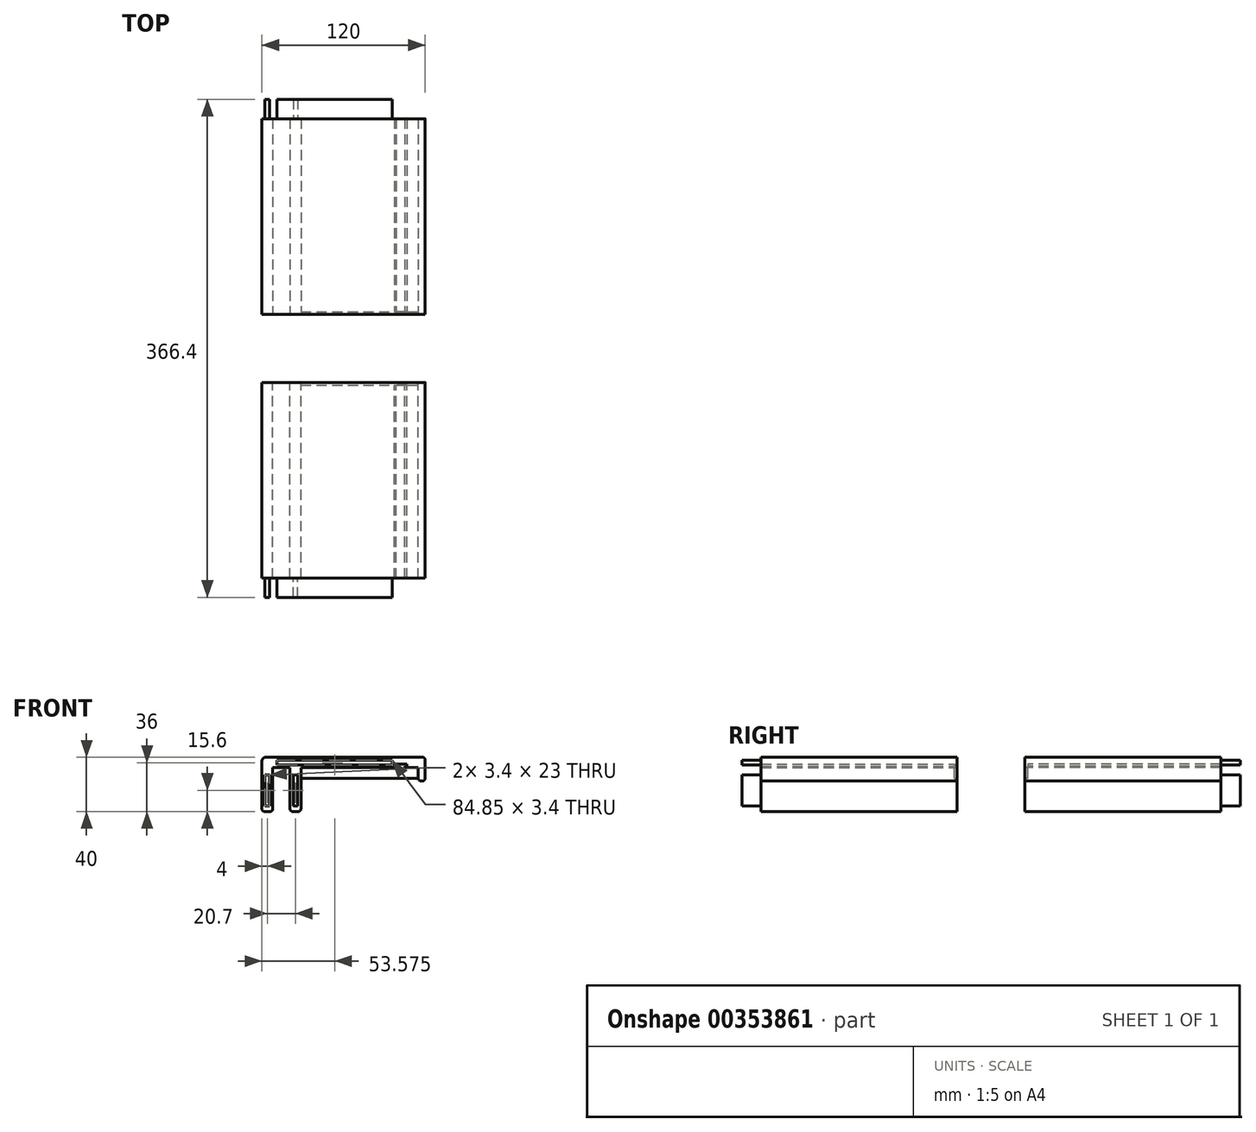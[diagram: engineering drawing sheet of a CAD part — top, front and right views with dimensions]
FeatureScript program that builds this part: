
annotation { "Feature Type Name" : "Feature", "Feature Type Description" : "" }
export const myFeature = defineFeature(function(context is Context, id is Id, definition is map)
    precondition{}
    {
        {
            var Q0;
            Q0=qCreatedBy(makeId("Front.planeOp"),FACE);
            var sketch = newSketch(context, id + "F0", { "sketchPlane" : qUnion([Q0])});
            skLineSegment(sketch, "E0", {"start": v(0, 2) * mm, "end": v(0, 37) * mm});
            skLineSegment(sketch, "E1", {"start": v(3, 40) * mm, "end": v(118, 40) * mm});
            skLineSegment(sketch, "E2", {"start": v(105, 32.4) * mm, "end": v(105, 33.4) * mm});
            skLineSegment(sketch, "E3", {"start": v(105, 33.4) * mm, "end": v(106.75, 33.4) * mm});
            skLineSegment(sketch, "E4", {"start": v(106.75, 33.4) * mm, "end": v(106.75, 34.8) * mm});
            skLineSegment(sketch, "E5", {"start": v(106.75, 34.8) * mm, "end": v(97.45, 34.8) * mm});
            skLineSegment(sketch, "E6", {"start": v(97.45, 34.8) * mm, "end": v(97.45, 33.4) * mm});
            skLineSegment(sketch, "E7", {"start": v(97.45, 33.4) * mm, "end": v(98.7, 33.4) * mm});
            skLineSegment(sketch, "E8", {"start": v(98.7, 33.4) * mm, "end": v(98.7, 32.4) * mm});
            skLineSegment(sketch, "E9", {"start": v(98.7, 32.4) * mm, "end": v(28.7, 32.4) * mm});
            skLineSegment(sketch, "E10", {"start": v(28.7, 32.4) * mm, "end": v(28.7, 2) * mm});
            skLineSegment(sketch, "E11", {"start": v(26.7, 0) * mm, "end": v(22.7, 0) * mm});
            skLineSegment(sketch, "E12", {"start": v(20.7, 2) * mm, "end": v(20.7, 32.4) * mm});
            skLineSegment(sketch, "E13", {"start": v(20.7, 32.4) * mm, "end": v(8, 32.4) * mm});
            skLineSegment(sketch, "E14", {"start": v(8, 32.4) * mm, "end": v(8, 2) * mm});
            skLineSegment(sketch, "E15", {"start": v(6, 0) * mm, "end": v(2, 0) * mm});
            skLineSegment(sketch, "E16", {"start": v(105, 32.4) * mm, "end": v(120, 32.4) * mm});
            skLineSegment(sketch, "E17", {"start": v(120, 38) * mm, "end": v(120, 32.4) * mm});
            skLineSegment(sketch, "E18", {"start": v(120, 32.4) * mm, "end": v(120, 24.4) * mm});
            skLineSegment(sketch, "E19", {"start": v(118, 22.4) * mm, "end": v(117, 22.4) * mm});
            skLineSegment(sketch, "E20", {"start": v(115, 24.4) * mm, "end": v(115, 32.4) * mm});
            skPoint(sketch, "E21.visualSharp", {"position": v(0, 40) * mm});
            skArc(sketch, "E21.filletArc", {"start": v(3, 40) * mm, "mid": v(0.88, 39.12) * mm, "end": v(0, 37) * mm});
            skPoint(sketch, "E22.visualSharp", {"position": v(0, 0) * mm});
            skArc(sketch, "E22.filletArc", {"start": v(0, 2) * mm, "mid": v(0.59, 0.59) * mm, "end": v(2, 0) * mm});
            skPoint(sketch, "E23.visualSharp", {"position": v(8, 0) * mm});
            skArc(sketch, "E23.filletArc", {"start": v(6, 0) * mm, "mid": v(7.41, 0.59) * mm, "end": v(8, 2) * mm});
            skPoint(sketch, "E24.visualSharp", {"position": v(20.7, 0) * mm});
            skArc(sketch, "E24.filletArc", {"start": v(20.7, 2) * mm, "mid": v(21.29, 0.59) * mm, "end": v(22.7, 0) * mm});
            skPoint(sketch, "E25.visualSharp", {"position": v(28.7, 0) * mm});
            skArc(sketch, "E25.filletArc", {"start": v(26.7, 0) * mm, "mid": v(28.11, 0.59) * mm, "end": v(28.7, 2) * mm});
            skPoint(sketch, "E26.visualSharp", {"position": v(120, 22.4) * mm});
            skArc(sketch, "E26.filletArc", {"start": v(118, 22.4) * mm, "mid": v(119.41, 23) * mm, "end": v(120, 24.4) * mm});
            skPoint(sketch, "E27.visualSharp", {"position": v(115, 22.4) * mm});
            skArc(sketch, "E27.filletArc", {"start": v(115, 24.4) * mm, "mid": v(115.59, 23) * mm, "end": v(117, 22.4) * mm});
            skPoint(sketch, "E28.visualSharp", {"position": v(120, 40) * mm});
            skArc(sketch, "E28.filletArc", {"start": v(120, 38) * mm, "mid": v(119.41, 39.41) * mm, "end": v(118, 40) * mm});
            skSolve(sketch);
        }
        {
            var Q0;
            Q0=makeQuery(id+"F0.imprint","IMPRINT",FACE,{"disambiguationData":[TD([[makeQuery(id+"F0.imprint","IMPRINT",EDGE,{"derivedFrom":sQuery(id+"F0.wireOp",EDGE,"E0")}),-1.0]])]});
            var Q1;
            {var subQ1=sQuery(id+"F0.wireOp",EDGE,"E18");Q1=makeQuery(id+"F0.imprint","IMPRINT",FACE,{"disambiguationData":[TD([[makeQuery(id+"F0.imprint","IMPRINT",EDGE,{"derivedFrom":subQ1}),-1.0]])]});}
            extrude(context, id + "F1", {"entities" : qUnion([Q0, Q1]), "depth" : 144 * mm});
        }
        {
            var Q0;
            Q0=makeQuery(id+"F1.opExtrude","CAP_FACE",FACE,{"disambiguationData":[OSD([sQuery(id+"F0.wireOp",EDGE,"E0"),sQuery(id+"F0.wireOp",EDGE,"E1"),sQuery(id+"F0.wireOp",EDGE,"E2"),sQuery(id+"F0.wireOp",EDGE,"E3"),sQuery(id+"F0.wireOp",EDGE,"E4"),sQuery(id+"F0.wireOp",EDGE,"E5"),sQuery(id+"F0.wireOp",EDGE,"E6"),sQuery(id+"F0.wireOp",EDGE,"E7"),sQuery(id+"F0.wireOp",EDGE,"E8"),sQuery(id+"F0.wireOp",EDGE,"E9"),sQuery(id+"F0.wireOp",EDGE,"E10"),sQuery(id+"F0.wireOp",EDGE,"E11"),sQuery(id+"F0.wireOp",EDGE,"E12"),sQuery(id+"F0.wireOp",EDGE,"E13"),sQuery(id+"F0.wireOp",EDGE,"E14"),sQuery(id+"F0.wireOp",EDGE,"E15"),sQuery(id+"F0.wireOp",EDGE,"E16"),sQuery(id+"F0.wireOp",EDGE,"E17"),sQuery(id+"F0.wireOp",EDGE,"E18"),sQuery(id+"F0.wireOp",EDGE,"E19"),sQuery(id+"F0.wireOp",EDGE,"E20"),sQuery(id+"F0.wireOp",EDGE,"E21.filletArc"),sQuery(id+"F0.wireOp",EDGE,"E22.filletArc"),sQuery(id+"F0.wireOp",EDGE,"E23.filletArc"),sQuery(id+"F0.wireOp",EDGE,"E24.filletArc"),sQuery(id+"F0.wireOp",EDGE,"E25.filletArc"),sQuery(id+"F0.wireOp",EDGE,"E26.filletArc"),sQuery(id+"F0.wireOp",EDGE,"E27.filletArc"),sQuery(id+"F0.wireOp",EDGE,"E28.filletArc")])],"isStart":false});
            var sketch = newSketch(context, id + "F2", { "sketchPlane" : qUnion([Q0])});
            skLineSegment(sketch, "E29.bottom", {"start": v(11.15, 37.7) * mm, "end": v(96, 37.7) * mm});
            skLineSegment(sketch, "E29.top", {"start": v(11.15, 34.3) * mm, "end": v(96, 34.3) * mm});
            skLineSegment(sketch, "E29.left", {"start": v(11.15, 37.7) * mm, "end": v(11.15, 34.3) * mm});
            skLineSegment(sketch, "E29.right", {"start": v(96, 37.7) * mm, "end": v(96, 34.3) * mm});
            skLineSegment(sketch, "E30.bottom", {"start": v(2.3, 27.1) * mm, "end": v(5.7, 27.1) * mm});
            skLineSegment(sketch, "E30.top", {"start": v(2.3, 4.1) * mm, "end": v(5.7, 4.1) * mm});
            skLineSegment(sketch, "E30.left", {"start": v(2.3, 27.1) * mm, "end": v(2.3, 4.1) * mm});
            skLineSegment(sketch, "E30.right", {"start": v(5.7, 27.1) * mm, "end": v(5.7, 4.1) * mm});
            skLineSegment(sketch, "E31.bottom", {"start": v(23, 27.1) * mm, "end": v(26.4, 27.1) * mm});
            skLineSegment(sketch, "E31.top", {"start": v(23, 4.1) * mm, "end": v(26.4, 4.1) * mm});
            skLineSegment(sketch, "E31.left", {"start": v(23, 27.1) * mm, "end": v(23, 4.1) * mm});
            skLineSegment(sketch, "E31.right", {"start": v(26.4, 27.1) * mm, "end": v(26.4, 4.1) * mm});
            skSolve(sketch);
        }
        {
            var Q0;
            Q0=makeQuery(id+"F2.imprint","IMPRINT",FACE,{"disambiguationData":[TD([[makeQuery(id+"F2.imprint","IMPRINT",EDGE,{"derivedFrom":sQuery(id+"F2.wireOp",EDGE,"E29.bottom")}),-1.0]])]});
            var Q1;
            Q1=makeQuery(id+"F2.imprint","IMPRINT",FACE,{"disambiguationData":[TD([[makeQuery(id+"F2.imprint","IMPRINT",EDGE,{"derivedFrom":sQuery(id+"F2.wireOp",EDGE,"E30.bottom")}),-1.0]])]});
            var Q2;
            Q2=makeQuery(id+"F2.imprint","IMPRINT",FACE,{"disambiguationData":[TD([[makeQuery(id+"F2.imprint","IMPRINT",EDGE,{"derivedFrom":sQuery(id+"F2.wireOp",EDGE,"E31.bottom")}),-1.0]])]});
            extrude(context, id + "F3", {"entities" : qUnion([Q0, Q1, Q2]), "operationType" : NewBodyOperationType.ADD, "depth" : 14.2 * mm});
        }
        {
            var Q0;
            Q0=makeQuery(id+"F1.opExtrude","CAP_FACE",FACE,{"disambiguationData":[OSD([sQuery(id+"F0.wireOp",EDGE,"E0"),sQuery(id+"F0.wireOp",EDGE,"E1"),sQuery(id+"F0.wireOp",EDGE,"E2"),sQuery(id+"F0.wireOp",EDGE,"E3"),sQuery(id+"F0.wireOp",EDGE,"E4"),sQuery(id+"F0.wireOp",EDGE,"E5"),sQuery(id+"F0.wireOp",EDGE,"E6"),sQuery(id+"F0.wireOp",EDGE,"E7"),sQuery(id+"F0.wireOp",EDGE,"E8"),sQuery(id+"F0.wireOp",EDGE,"E9"),sQuery(id+"F0.wireOp",EDGE,"E10"),sQuery(id+"F0.wireOp",EDGE,"E11"),sQuery(id+"F0.wireOp",EDGE,"E12"),sQuery(id+"F0.wireOp",EDGE,"E13"),sQuery(id+"F0.wireOp",EDGE,"E14"),sQuery(id+"F0.wireOp",EDGE,"E15"),sQuery(id+"F0.wireOp",EDGE,"E16"),sQuery(id+"F0.wireOp",EDGE,"E17"),sQuery(id+"F0.wireOp",EDGE,"E18"),sQuery(id+"F0.wireOp",EDGE,"E19"),sQuery(id+"F0.wireOp",EDGE,"E20"),sQuery(id+"F0.wireOp",EDGE,"E21.filletArc"),sQuery(id+"F0.wireOp",EDGE,"E22.filletArc"),sQuery(id+"F0.wireOp",EDGE,"E23.filletArc"),sQuery(id+"F0.wireOp",EDGE,"E24.filletArc"),sQuery(id+"F0.wireOp",EDGE,"E25.filletArc"),sQuery(id+"F0.wireOp",EDGE,"E26.filletArc"),sQuery(id+"F0.wireOp",EDGE,"E27.filletArc"),sQuery(id+"F0.wireOp",EDGE,"E28.filletArc")])],"isStart":true});
            var sketch = newSketch(context, id + "F4", { "sketchPlane" : qUnion([Q0])});
            skLineSegment(sketch, "E32", {"start": v(-105, 32.4) * mm, "end": v(-105, 33.4) * mm});
            skLineSegment(sketch, "E33", {"start": v(-105, 33.4) * mm, "end": v(-106.75, 33.4) * mm});
            skLineSegment(sketch, "E34", {"start": v(-106.75, 33.4) * mm, "end": v(-106.75, 34.8) * mm});
            skLineSegment(sketch, "E35", {"start": v(-106.75, 34.8) * mm, "end": v(-97.45, 34.8) * mm});
            skLineSegment(sketch, "E36", {"start": v(-97.45, 34.8) * mm, "end": v(-97.45, 33.4) * mm});
            skLineSegment(sketch, "E37", {"start": v(-97.45, 33.4) * mm, "end": v(-98.7, 33.4) * mm});
            skLineSegment(sketch, "E38", {"start": v(-98.7, 33.4) * mm, "end": v(-98.7, 32.4) * mm});
            skLineSegment(sketch, "E39", {"start": v(-98.7, 32.4) * mm, "end": v(-105, 32.4) * mm});
            skSolve(sketch);
        }
        {
            var Q0;
            Q0 = qSketchRegion(id + "F4", true);
            extrude(context, id + "F5", {"entities" : qUnion([Q0]), "operationType" : NewBodyOperationType.ADD, "oppositeDirection" : true, "depth" : 2 * mm});
        }
        {
            var Q0;
            Q0=makeQuery(id+"F5.boolean.opBoolean","MERGE",FACE,{"derivedFrom":[makeQuery(id+"F1.opExtrude","SWEPT_FACE",FACE,{"disambiguationData":[OSD([sQuery(id+"F0.wireOp",EDGE,"E9")])]}),makeQuery(id+"F1.opExtrude","SWEPT_FACE",FACE,{"disambiguationData":[OSD([sQuery(id+"F0.wireOp",EDGE,"E16")])]}),makeQuery(id+"F5.opExtrude","SWEPT_FACE",FACE,{"disambiguationData":[OSD([sQuery(id+"F4.wireOp",EDGE,"E39")])]})]});
            var sketch = newSketch(context, id + "F6", { "sketchPlane" : qUnion([Q0])});
            skLineSegment(sketch, "E40.bottom", {"start": v(115, 0) * mm, "end": v(28.7, 0) * mm});
            skLineSegment(sketch, "E40.top", {"start": v(115, 2) * mm, "end": v(28.7, 2) * mm});
            skLineSegment(sketch, "E40.left", {"start": v(115, 0) * mm, "end": v(115, 2) * mm});
            skLineSegment(sketch, "E40.right", {"start": v(28.7, 0) * mm, "end": v(28.7, 2) * mm});
            skSolve(sketch);
        }
        {
            var Q0;
            Q0=makeQuery(id+"F6.imprint","IMPRINT",FACE,{"disambiguationData":[TD([[makeQuery(id+"F6.imprint","IMPRINT",EDGE,{"derivedFrom":sQuery(id+"F6.wireOp",EDGE,"E40.bottom")}),-1.0]])]});
            var Q1;
            Q1=makeQuery(id+"F1.opExtrude","CAP_VERTEX",VERTEX,{"disambiguationData":[OSD([sQuery(id+"F0.wireOp",EDGE,"E20"),sQuery(id+"F0.wireOp",EDGE,"E27.filletArc")])],"isStart":true});
            extrude(context, id + "F7", {"entities" : qUnion([Q0]), "operationType" : NewBodyOperationType.ADD, "endBound" : BoundingType.UP_TO_VERTEX, "endBoundEntityVertex" : qUnion([Q1]), "depth" : 25 * mm});
        }
        {
            var Q0;
            Q0=qCreatedBy(makeId("Front.planeOp"),FACE);
            cPlane(context, id + "F8", {"entities" : qUnion([Q0]), "cplaneType" : CPlaneType.OFFSET, "offset" : 25 * mm, "oppositeDirection" : true, "width" : 150 * mm, "height" : 150 * mm});
        }
        {
            var Q0;
            Q0=makeQuery(id+"F1.opExtrude","SWEPT_BODY",BODY,{"disambiguationData":[OSD([sQuery(id+"F0.wireOp",EDGE,"E0"),sQuery(id+"F0.wireOp",EDGE,"E1"),sQuery(id+"F0.wireOp",EDGE,"E2"),sQuery(id+"F0.wireOp",EDGE,"E3"),sQuery(id+"F0.wireOp",EDGE,"E4"),sQuery(id+"F0.wireOp",EDGE,"E5"),sQuery(id+"F0.wireOp",EDGE,"E6"),sQuery(id+"F0.wireOp",EDGE,"E7"),sQuery(id+"F0.wireOp",EDGE,"E8"),sQuery(id+"F0.wireOp",EDGE,"E9"),sQuery(id+"F0.wireOp",EDGE,"E10"),sQuery(id+"F0.wireOp",EDGE,"E11"),sQuery(id+"F0.wireOp",EDGE,"E12"),sQuery(id+"F0.wireOp",EDGE,"E13"),sQuery(id+"F0.wireOp",EDGE,"E14"),sQuery(id+"F0.wireOp",EDGE,"E15"),sQuery(id+"F0.wireOp",EDGE,"E16"),sQuery(id+"F0.wireOp",EDGE,"E17"),sQuery(id+"F0.wireOp",EDGE,"E18"),sQuery(id+"F0.wireOp",EDGE,"E19"),sQuery(id+"F0.wireOp",EDGE,"E20"),sQuery(id+"F0.wireOp",EDGE,"E21.filletArc"),sQuery(id+"F0.wireOp",EDGE,"E22.filletArc"),sQuery(id+"F0.wireOp",EDGE,"E23.filletArc"),sQuery(id+"F0.wireOp",EDGE,"E24.filletArc"),sQuery(id+"F0.wireOp",EDGE,"E25.filletArc"),sQuery(id+"F0.wireOp",EDGE,"E26.filletArc"),sQuery(id+"F0.wireOp",EDGE,"E27.filletArc"),sQuery(id+"F0.wireOp",EDGE,"E28.filletArc")])]});
            var Q1;
            Q1=qCreatedBy(id+"F8.planeOp",FACE);
            mirror(context, id + "F9", {"entities" : qUnion([Q0]), "mirrorPlane" : qUnion([Q1])});
        }
    });
